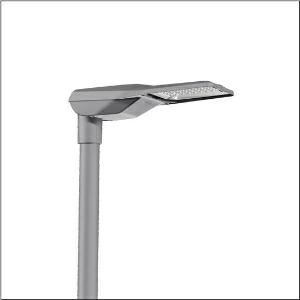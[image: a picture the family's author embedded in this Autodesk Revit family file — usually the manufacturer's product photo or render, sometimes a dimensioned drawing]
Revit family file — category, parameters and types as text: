
# Revit family: streetlight_sl_21_iq_mini___st0_8a_5xe2c21d08hb_7297
name_source: partatom
category: Lighting Fixtures
units: mm (PartAtom-declared; Revit-internal decimal feet)

## family parameters
Cut with Voids When Loaded = No
Host = Face
Light Source = No
Part Type = Normal
Room Calculation Point = No
Round Connector Dimension = Use Diameter
Shared = No

## types (1)
- --- (1 x LED, 7830 lm, 70.9 W, 2200K)
    Apparent Load = 71 VA
    CIE Flux Codes = 38 75 97 100 100
    Color Rendering = 70
    Color Temperature = 2200K
    Default Elevation = 1800 mm
    Description = Streetlight SL 21 iQ mini, mast luminaire, primary light control with lens, of PMMA, primary optical cover: cover, of toughened safety glass, transparent, light distribution: ST0.8a, light emission: direct distribution, primary light characteristic: asymmetric, installation type: post-top, side-entry, LED, High Power LED, rated luminous flux: 7.830lm, luminous efficacy: 110lm/W, light colour: 722, colour temperature: 2200K, control: Auto-Match, Temp-Guard, Lumen-Switch, Night-Set, Smart-Wire, Light-Fading, Desk-Remote (wireless, voltage-free reading and setting of iQ features in the workshop via application-optimized NFC function/RFID function), optimised constant luminous flux control (CLO 2.0), presetting dimming linear, mains connection: 220..240V, AC, 50/60Hz, start of lifetime: 71W, end of service life: 75W, reduction: 31W, luminaire housing, of diecast aluminium, powder-coated, Siteco® metallic grey (DB 702S), corrosivity category C5 mid according to DIN EN ISO 12944, please order mast flange separately, inclination adjustable: 0°, 5°, 10°, 15°, sealing non-destructively replaceable, multi-level sealing system, length: 628mm, width: 235mm, height: 110mm, mast flange for spigot size: 42mm (side-entry): 5XC10008XM4, 60/48mm (side-entry/post-top): 5XC10108XM2, 76/60mm (side-entry/post-top): 5XC10108XM1, protection rating (complete): IP66, insulation class (complete): insulation class II (safety insulation), certification: CE, ENEC, ENEC+, VDE, impact resistance: IK09, permissible operating ambient temperature for outdoor applications: -40..+50°C, standard-compliant lighting for roads and squares, packaging unit: 1 piece

Light Distribution: ST0.8a
    Height = 110 mm
    Lamp = 1 x LED
    Lamp Light Flux = 7830 lm
    Lamp Power = 70.9 W
    Lamp count = 1
    Length = 625 mm
    Luminous efficacy = 110 lm/W
    Manufacturer = Siteco
    ModVariant = No
    Model = 5XE2C21D08HB
    Number of Poles = 1
    OnlyDefault = Yes
    Power Factor = 1
    Product Name = Streetlight SL 21 iQ mini | ST0.8a
    Product group = mast luminaire | pylon top
    ProductGroupID = 6100
    Protection Class = Protection class II
    Protection Degree = IP 66
    RLX_Detail_Level = 1
    RLX_Emergency_Light_Flux = 0 lm
    RLX_Emergency_Type = 0
    RLX_Emergency_Type_DB = No
    RlxData = <blob elided: 92409 chars, md5=392987d4>
    Socket = socket
    Standby Power = 0 W
    System Light Flux = 7830 lm
    System Power = 71 W
    Type Comments = factory setting: luminous flux: 100 % | dim-lin: 254 | 711 mA
    Type Image = l_1003519.jpg
    URL = http://relux.com
    VarID = @adj_089887
    Voltage = 0 V
    Weight = 0.00 kg
    Width = 234 mm

## geometry (parser evidence)
native form markers: Blend x4, Sweep x12
no freeform markers — native parametric forms only
